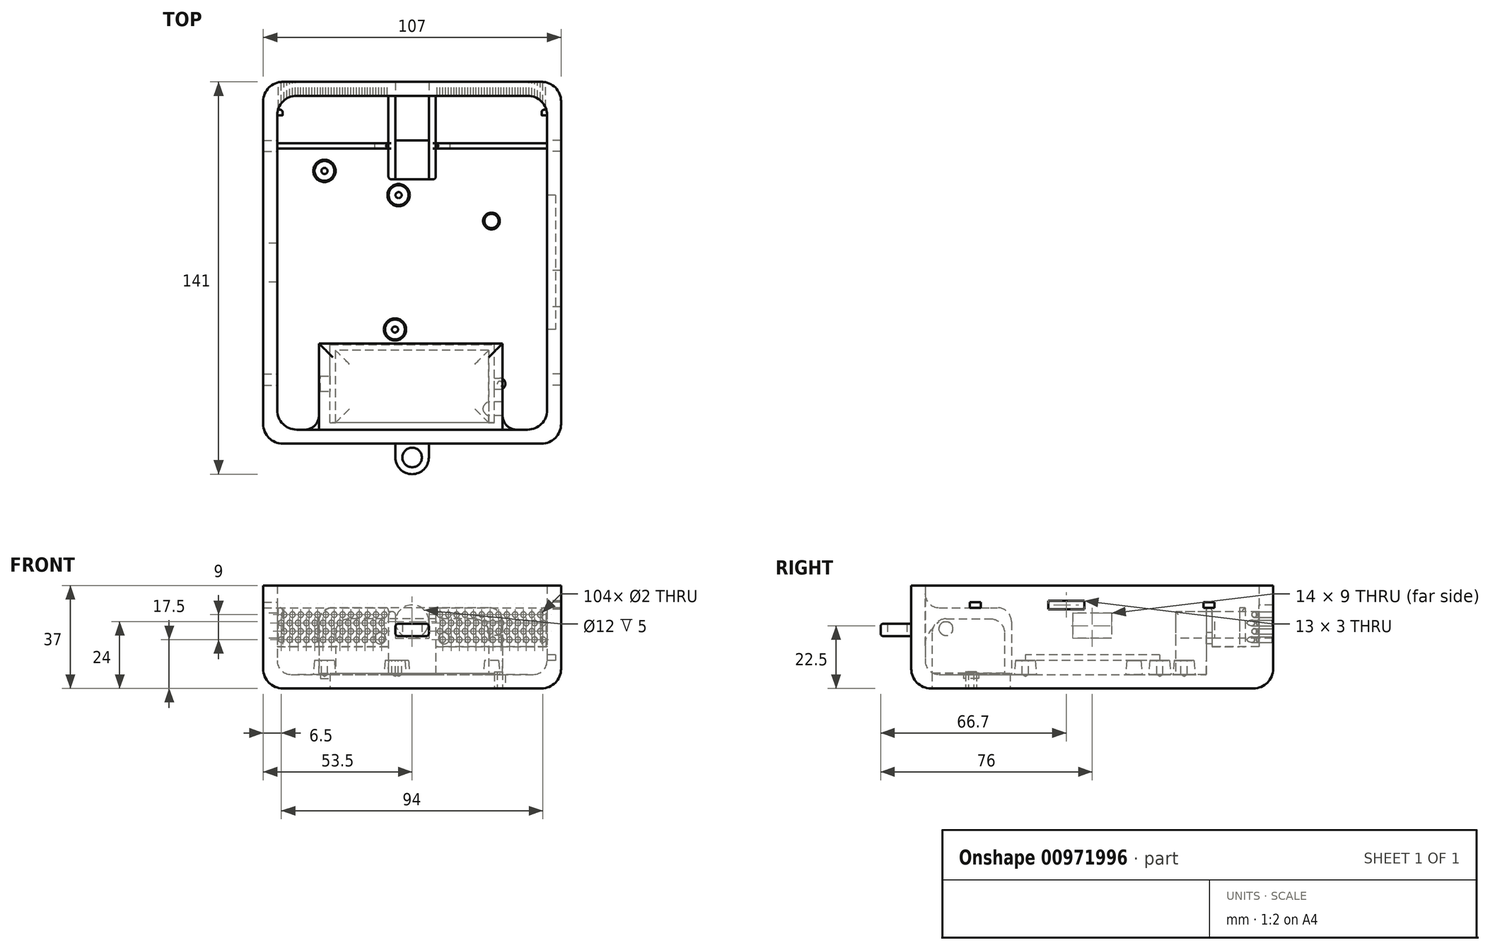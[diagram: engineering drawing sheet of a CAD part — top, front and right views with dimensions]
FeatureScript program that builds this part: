
annotation { "Feature Type Name" : "Feature", "Feature Type Description" : "" }
export const myFeature = defineFeature(function(context is Context, id is Id, definition is map)
    precondition{}
    {
        {
            var Q0;
            Q0=qCreatedBy(makeId("Top.planeOp"),FACE);
            var sketch = newSketch(context, id + "F0", { "sketchPlane" : qUnion([Q0])});
            skLineSegment(sketch, "E0.bottom", {"start": v(48.5, -60) * mm, "end": v(-48.5, -60) * mm});
            skLineSegment(sketch, "E0.top", {"start": v(48.5, 60) * mm, "end": v(-48.5, 60) * mm});
            skLineSegment(sketch, "E0.left", {"start": v(48.5, -60) * mm, "end": v(48.5, 60) * mm});
            skLineSegment(sketch, "E0.right", {"start": v(-48.5, -60) * mm, "end": v(-48.5, 60) * mm});
            skPoint(sketch, "E0.middle", {"position": v(0, 0) * mm});
            skSolve(sketch);
        }
        {
            var Q0;
            Q0 = qSketchRegion(id + "F0", true);
            extrude(context, id + "F1", {"entities" : qUnion([Q0]), "depth" : 32 * mm, "offsetDistance" : 25 * mm});
        }
        {
            var Q0;
            Q0=makeQuery(id+"F1.opExtrude","CAP_FACE",FACE,{"disambiguationData":[OSD([sQuery(id+"F0.wireOp",EDGE,"E0.bottom"),sQuery(id+"F0.wireOp",EDGE,"E0.top"),sQuery(id+"F0.wireOp",EDGE,"E0.left"),sQuery(id+"F0.wireOp",EDGE,"E0.right")])],"isStart":false});
            shell(context, id + "F2", {"entities" : qUnion([Q0]), "thickness" : 5 * mm, "oppositeDirection" : true});
        }
        {
            var Q0;
            Q0=qCreatedBy(makeId("Top.planeOp"),FACE);
            cPlane(context, id + "F3", {"entities" : qUnion([Q0]), "cplaneType" : CPlaneType.OFFSET, "offset" : 16 * mm, "width" : 150 * mm, "height" : 150 * mm});
        }
        {
            var Q0;
            Q0=qCreatedBy(id+"F3.planeOp",FACE);
            var sketch = newSketch(context, id + "F4", { "sketchPlane" : qUnion([Q0])});
            skLineSegment(sketch, "E1.bottom", {"start": v(6, -70) * mm, "end": v(-6, -70) * mm});
            skLineSegment(sketch, "E1.top", {"start": v(6, -65) * mm, "end": v(-6, -65) * mm});
            skLineSegment(sketch, "E1.left", {"start": v(6, -70) * mm, "end": v(6, -65) * mm});
            skLineSegment(sketch, "E1.right", {"start": v(-6, -70) * mm, "end": v(-6, -65) * mm});
            skArc(sketch, "E2", {"start": v(-6, -70) * mm, "mid": v(0, -76) * mm, "end": v(6, -70) * mm});
            skCircle(sketch, "E3", {"center": v(0, -70) * mm, "radius": 3.5 * mm});
            skSolve(sketch);
        }
        {
            var Q0;
            Q0 = qSketchRegion(id + "F4", true);
            extrude(context, id + "F5", {"entities" : qUnion([Q0]), "operationType" : NewBodyOperationType.ADD, "depth" : 2.25 * mm, "offsetDistance" : 25 * mm, "hasSecondDirection" : true, "secondDirectionOppositeDirection" : true, "secondDirectionDepth" : 2.25 * mm});
        }
        {
            var Q0;
            Q0=makeQuery(id+"F2.opShell","OFFSET_FACE",FACE,{"disambiguationData":[OSD([sQuery(id+"F0.wireOp",EDGE,"E0.bottom"),sQuery(id+"F0.wireOp",EDGE,"E0.top"),sQuery(id+"F0.wireOp",EDGE,"E0.left"),sQuery(id+"F0.wireOp",EDGE,"E0.right"),sQuery(id+"F0.wireOp",EDGE,"ri5jnIwm-DSlt-X9KJ-Zgm1-c5zNFrCCeeFj.top"),sQuery(id+"F0.wireOp",EDGE,"ri5jnIwm-DSlt-X9KJ-Zgm1-c5zNFrCCeeFj.left"),sQuery(id+"F0.wireOp",EDGE,"ri5jnIwm-DSlt-X9KJ-Zgm1-c5zNFrCCeeFj.right")])]});
            var sketch = newSketch(context, id + "F6", { "sketchPlane" : qUnion([Q0])});
            skLineSegment(sketch, "E4.bottom", {"start": v(-33.5, -60) * mm, "end": v(32.5, -60) * mm});
            skLineSegment(sketch, "E4.top", {"start": v(-33.5, -29) * mm, "end": v(32.5, -29) * mm});
            skLineSegment(sketch, "E4.left", {"start": v(-33.5, -60) * mm, "end": v(-33.5, -29) * mm});
            skLineSegment(sketch, "E4.right", {"start": v(32.5, -60) * mm, "end": v(32.5, -29) * mm});
            skLineSegment(sketch, "E5.bottom", {"start": v(27.5, -57.5) * mm, "end": v(-27.5, -57.5) * mm});
            skLineSegment(sketch, "E5.top", {"start": v(27.5, -31.5) * mm, "end": v(-27.5, -31.5) * mm});
            skLineSegment(sketch, "E5.left", {"start": v(27.5, -57.5) * mm, "end": v(27.5, -31.5) * mm});
            skLineSegment(sketch, "E5.right", {"start": v(-27.5, -57.5) * mm, "end": v(-27.5, -31.5) * mm});
            skPoint(sketch, "E5.middle", {"position": v(0, -44.5) * mm});
            skPoint(sketch, "E6", {"position": v(-33.5, -44.5) * mm});
            skSolve(sketch);
        }
        {
            var Q0;
            Q0=makeQuery(id+"F6.imprint","IMPRINT",FACE,{"disambiguationData":[TD([[makeQuery(id+"F6.imprint","IMPRINT",EDGE,{"derivedFrom":sQuery(id+"F6.wireOp",EDGE,"E5.bottom")}),-1.0]])]});
            var Q1;
            Q1=makeQuery(id+"F6.imprint","IMPRINT",FACE,{"disambiguationData":[TD([[makeQuery(id+"F6.imprint","IMPRINT",EDGE,{"derivedFrom":sQuery(id+"F6.wireOp",EDGE,"E4.bottom")}),-1.0]])]});
            extrude(context, id + "F7", {"entities" : qUnion([Q0, Q1]), "operationType" : NewBodyOperationType.ADD, "depth" : 24 * mm, "offsetDistance" : 25 * mm});
        }
        {
            var Q0;
            Q0=makeQuery(id+"F6.imprint","IMPRINT",FACE,{"disambiguationData":[TD([[makeQuery(id+"F6.imprint","IMPRINT",EDGE,{"derivedFrom":sQuery(id+"F6.wireOp",EDGE,"E5.bottom")}),-1.0]])]});
            var Q1;
            Q1=makeQuery(id+"F1.opExtrude","CAP_FACE",FACE,{"disambiguationData":[OSD([sQuery(id+"F0.wireOp",EDGE,"E0.bottom"),sQuery(id+"F0.wireOp",EDGE,"E0.top"),sQuery(id+"F0.wireOp",EDGE,"E0.left"),sQuery(id+"F0.wireOp",EDGE,"E0.right"),sQuery(id+"F0.wireOp",EDGE,"ri5jnIwm-DSlt-X9KJ-Zgm1-c5zNFrCCeeFj.top"),sQuery(id+"F0.wireOp",EDGE,"ri5jnIwm-DSlt-X9KJ-Zgm1-c5zNFrCCeeFj.left"),sQuery(id+"F0.wireOp",EDGE,"ri5jnIwm-DSlt-X9KJ-Zgm1-c5zNFrCCeeFj.right")])],"isStart":true});
            extrude(context, id + "F8", {"entities" : qUnion([Q0]), "operationType" : NewBodyOperationType.REMOVE, "depth" : 20 * mm, "offsetDistance" : 25 * mm, "hasSecondDirection" : true, "secondDirectionBound" : SecondDirectionBoundingType.UP_TO_SURFACE, "secondDirectionOppositeDirection" : true, "secondDirectionDepth" : 25 * mm, "secondDirectionBoundEntityFace" : qUnion([Q1])});
        }
        {
            var Q0;
            Q0=makeQuery(id+"F1.opExtrude","CAP_FACE",FACE,{"disambiguationData":[OSD([sQuery(id+"F0.wireOp",EDGE,"E0.bottom"),sQuery(id+"F0.wireOp",EDGE,"E0.top"),sQuery(id+"F0.wireOp",EDGE,"E0.left"),sQuery(id+"F0.wireOp",EDGE,"E0.right")])],"isStart":true});
            var sketch = newSketch(context, id + "F9", { "sketchPlane" : qUnion([Q0])});
            skLineSegment(sketch, "E7.bottom", {"start": v(-29.5, 57.5) * mm, "end": v(29.5, 57.5) * mm});
            skLineSegment(sketch, "E7.top", {"start": v(-29.5, 29.5) * mm, "end": v(29.5, 29.5) * mm});
            skLineSegment(sketch, "E7.left", {"start": v(-29.5, 57.5) * mm, "end": v(-29.5, 29.5) * mm});
            skLineSegment(sketch, "E7.right", {"start": v(29.5, 57.5) * mm, "end": v(29.5, 29.5) * mm});
            skSolve(sketch);
        }
        {
            var Q0;
            Q0 = qSketchRegion(id + "F9", true);
            extrude(context, id + "F10", {"entities" : qUnion([Q0]), "operationType" : NewBodyOperationType.REMOVE, "oppositeDirection" : true, "depth" : 5.5 * mm, "offsetDistance" : 25 * mm});
        }
        {
            var Q0;
            Q0=makeQuery(id+"F10.boolean.opBoolean","COPY",FACE,{"derivedFrom":makeQuery(id+"F10.opExtrude","SWEPT_FACE",FACE,{"disambiguationData":[OSD([sQuery(id+"F9.wireOp",EDGE,"E7.left")])]})});
            var sketch = newSketch(context, id + "F11", { "sketchPlane" : qUnion([Q0])});
            skLineSegment(sketch, "E8.bottom", {"start": v(-40.75, 0.5) * mm, "end": v(-46.25, 0.5) * mm});
            skLineSegment(sketch, "E8.top", {"start": v(-40.75, -1.5) * mm, "end": v(-46.25, -1.5) * mm});
            skLineSegment(sketch, "E8.left", {"start": v(-40.75, 0.5) * mm, "end": v(-40.75, -1.5) * mm});
            skLineSegment(sketch, "E8.right", {"start": v(-46.25, 0.5) * mm, "end": v(-46.25, -1.5) * mm});
            skPoint(sketch, "E9", {"position": v(-43.5, 0.5) * mm});
            skSolve(sketch);
        }
        {
            var Q0;
            Q0 = qSketchRegion(id + "F11", true);
            extrude(context, id + "F12", {"entities" : qUnion([Q0]), "operationType" : NewBodyOperationType.REMOVE, "oppositeDirection" : true, "depth" : 3.5 * mm, "offsetDistance" : 25 * mm});
        }
        {
            var Q0;
            Q0=makeQuery(id+"F1.opExtrude","CAP_FACE",FACE,{"disambiguationData":[OSD([sQuery(id+"F0.wireOp",EDGE,"E0.bottom"),sQuery(id+"F0.wireOp",EDGE,"E0.top"),sQuery(id+"F0.wireOp",EDGE,"E0.left"),sQuery(id+"F0.wireOp",EDGE,"E0.right")])],"isStart":true});
            var sketch = newSketch(context, id + "F13", { "sketchPlane" : qUnion([Q0])});
            skLineSegment(sketch, "E10.bottom", {"start": v(29.5, 45.5) * mm, "end": v(31.5, 45.5) * mm});
            skLineSegment(sketch, "E10.top", {"start": v(29.5, 41.5) * mm, "end": v(31.5, 41.5) * mm});
            skLineSegment(sketch, "E10.left", {"start": v(29.5, 45.5) * mm, "end": v(29.5, 41.5) * mm});
            skLineSegment(sketch, "E10.right", {"start": v(31.5, 45.5) * mm, "end": v(31.5, 41.5) * mm});
            skArc(sketch, "E11", {"start": v(31.5, 41.5) * mm, "mid": v(33.5, 43.5) * mm, "end": v(31.5, 45.5) * mm});
            skCircle(sketch, "E12", {"center": v(31.5, 43.5) * mm, "radius": 0.9 * mm});
            skSolve(sketch);
        }
        {
            var Q0;
            Q0 = qSketchRegion(id + "F13", true);
            var Q1;
            {var subQ0=sQuery(id+"F13.wireOp",EDGE,"E12");var subQ1=sQuery(id+"F13.wireOp",EDGE,"E10.right");var subQ2=makeQuery(id+"F13.imprint","INTERSECT",VERTEX,{"disambiguationData":[OD(0.0)],"derivedFrom":[subQ1,subQ0]});Q1=makeQuery(id+"F13.imprint","IMPRINT",FACE,{"disambiguationData":[TD([[makeQuery(id+"F13.imprint","IMPRINT",EDGE,{"disambiguationData":[TD([[subQ2,-1.0]])],"derivedFrom":subQ1}),-1.0]])]});}
            var Q2;
            {var subQ0=sQuery(id+"F13.wireOp",EDGE,"E12");var subQ1=sQuery(id+"F13.wireOp",EDGE,"E10.right");var subQ2=makeQuery(id+"F13.imprint","INTERSECT",VERTEX,{"disambiguationData":[OD(0.0)],"derivedFrom":[subQ1,subQ0]});Q2=makeQuery(id+"F13.imprint","IMPRINT",FACE,{"disambiguationData":[TD([[makeQuery(id+"F13.imprint","IMPRINT",EDGE,{"disambiguationData":[TD([[subQ2,-1.0]])],"derivedFrom":subQ1}),1.0]])]});}
            extrude(context, id + "F14", {"entities" : qUnion([Q0, Q1, Q2]), "operationType" : NewBodyOperationType.REMOVE, "oppositeDirection" : true, "depth" : 3.5 * mm, "offsetDistance" : 25 * mm});
        }
        {
            var Q0;
            {var subQ0=sQuery(id+"F13.wireOp",EDGE,"E12");var subQ1=sQuery(id+"F13.wireOp",EDGE,"E10.right");var subQ2=makeQuery(id+"F13.imprint","INTERSECT",VERTEX,{"disambiguationData":[OD(0.0)],"derivedFrom":[subQ1,subQ0]});Q0=makeQuery(id+"F13.imprint","IMPRINT",FACE,{"disambiguationData":[TD([[makeQuery(id+"F13.imprint","IMPRINT",EDGE,{"disambiguationData":[TD([[subQ2,-1.0]])],"derivedFrom":subQ1}),-1.0]])]});}
            var Q1;
            {var subQ0=sQuery(id+"F13.wireOp",EDGE,"E12");var subQ1=sQuery(id+"F13.wireOp",EDGE,"E10.right");var subQ2=makeQuery(id+"F13.imprint","INTERSECT",VERTEX,{"disambiguationData":[OD(0.0)],"derivedFrom":[subQ1,subQ0]});Q1=makeQuery(id+"F13.imprint","IMPRINT",FACE,{"disambiguationData":[TD([[makeQuery(id+"F13.imprint","IMPRINT",EDGE,{"disambiguationData":[TD([[subQ2,-1.0]])],"derivedFrom":subQ1}),1.0]])]});}
            var Q2;
            Q2=makeQuery(id+"F2.opShell","OFFSET_FACE",FACE,{"disambiguationData":[OSD([sQuery(id+"F0.wireOp",EDGE,"E0.bottom"),sQuery(id+"F0.wireOp",EDGE,"E0.top"),sQuery(id+"F0.wireOp",EDGE,"E0.left"),sQuery(id+"F0.wireOp",EDGE,"E0.right")])]});
            extrude(context, id + "F15", {"entities" : qUnion([Q0, Q1]), "operationType" : NewBodyOperationType.REMOVE, "oppositeDirection" : true, "depth" : 6 * mm, "endBoundEntityFace" : qUnion([Q2]), "offsetDistance" : 25 * mm});
        }
        {
            var Q0;
            Q0=makeQuery(id+"F2.opShell","OFFSET_FACE",FACE,{"disambiguationData":[OSD([sQuery(id+"F0.wireOp",EDGE,"E0.bottom"),sQuery(id+"F0.wireOp",EDGE,"E0.top"),sQuery(id+"F0.wireOp",EDGE,"E0.left"),sQuery(id+"F0.wireOp",EDGE,"E0.right")])]});
            var sketch = newSketch(context, id + "F16", { "sketchPlane" : qUnion([Q0])});
            skCircle(sketch, "E13", {"center": v(-4.86, 24.3) * mm, "radius": 4 * mm});
            skCircle(sketch, "E14", {"center": v(-6.16, -24) * mm, "radius": 4 * mm});
            skCircle(sketch, "E15", {"center": v(-31.5, 33) * mm, "radius": 4 * mm});
            skCircle(sketch, "E16", {"center": v(28.5, 15) * mm, "radius": 3 * mm});
            skSolve(sketch);
        }
        {
            var Q0;
            Q0 = qSketchRegion(id + "F16", true);
            extrude(context, id + "F17", {"entities" : qUnion([Q0]), "operationType" : NewBodyOperationType.ADD, "depth" : 5 * mm, "offsetDistance" : 25 * mm, "hasDraft" : true, "draftAngle" : 5 * degree, "draftPullDirection" : true});
        }
        {
            var Q0;
            Q0=makeQuery(id+"F17.opExtrude","CAP_FACE",FACE,{"disambiguationData":[OSD([sQuery(id+"F16.wireOp",EDGE,"E13")])],"isStart":false});
            var sketch = newSketch(context, id + "F18", { "sketchPlane" : qUnion([Q0])});
            skPoint(sketch, "E17", {"position": v(-6.16, -24) * mm});
            skPoint(sketch, "E18", {"position": v(-4.86, 24.3) * mm});
            skPoint(sketch, "E19", {"position": v(-31.5, 33) * mm});
            skSolve(sketch);
        }
        {
            var Q0;
            Q0=sQuery(id+"F18.wireOp",VERTEX,"9129957a-feda-4fe3-816d-9d5734e9e23f");
            var Q1;
            Q1=sQuery(id+"F18.wireOp",VERTEX,"4356859b-67c6-456f-994f-b7b154a957ab");
            var Q2;
            Q2=sQuery(id+"F18.wireOp",VERTEX,"E17");
            var Q3;
            Q3=sQuery(id+"F18.wireOp",VERTEX,"E18");
            var Q4;
            Q4=sQuery(id+"F18.wireOp",VERTEX,"E19");
            var Q5;
            Q5=makeQuery(id+"F1.opExtrude","SWEPT_BODY",BODY,{"disambiguationData":[OSD([sQuery(id+"F0.wireOp",EDGE,"E0.bottom"),sQuery(id+"F0.wireOp",EDGE,"E0.top"),sQuery(id+"F0.wireOp",EDGE,"E0.left"),sQuery(id+"F0.wireOp",EDGE,"E0.right")])]});
            hole(context, id + "F19", {"style" : HoleStyle.SIMPLE, "endStyle" : HoleEndStyle.BLIND, "holeDiameter" : 2.2 * mm, "majorDiameter" : 5 * mm, "holeDepth" : 5 * mm, "isTappedThrough" : true, "tappedDepth" : 12 * mm, "tapClearance" : 3, "locations" : qUnion([Q0, Q1, Q2, Q3, Q4]), "scope" : qUnion([Q5])});
        }
        {
            var Q0;
            Q0=makeQuery(id+"F2.opShell","OFFSET_FACE",FACE,{"disambiguationData":[OSD([sQuery(id+"F0.wireOp",EDGE,"E0.left")])]});
            var sketch = newSketch(context, id + "F20", { "sketchPlane" : qUnion([Q0])});
            skLineSegment(sketch, "E20.bottom", {"start": v(-24.3, 7) * mm, "end": v(24, 7) * mm});
            skLineSegment(sketch, "E20.top", {"start": v(-24.3, 5) * mm, "end": v(24, 5) * mm});
            skLineSegment(sketch, "E20.left", {"start": v(-24.3, 7) * mm, "end": v(-24.3, 5) * mm});
            skLineSegment(sketch, "E20.right", {"start": v(24, 7) * mm, "end": v(24, 5) * mm});
            skSolve(sketch);
        }
        {
            var Q0;
            Q0 = qSketchRegion(id + "F20", true);
            extrude(context, id + "F21", {"entities" : qUnion([Q0]), "operationType" : NewBodyOperationType.REMOVE, "oppositeDirection" : true, "depth" : 3 * mm, "offsetDistance" : 25 * mm});
        }
        {
            var Q0;
            Q0=makeQuery(id+"F8.boolean.opBoolean","COPY",FACE,{"derivedFrom":makeQuery(id+"F8.opExtrude","SWEPT_FACE",FACE,{"disambiguationData":[OSD([sQuery(id+"F6.wireOp",EDGE,"E5.left")])]})});
            var sketch = newSketch(context, id + "F22", { "sketchPlane" : qUnion([Q0])});
            skCircle(sketch, "E21", {"center": v(52.5, 16.5) * mm, "radius": 2.5 * mm});
            skSolve(sketch);
        }
        {
            var Q0;
            Q0 = qSketchRegion(id + "F22", true);
            var Q1;
            Q1=makeQuery(id+"F7.opExtrude","SWEPT_FACE",FACE,{"disambiguationData":[OSD([sQuery(id+"F6.wireOp",EDGE,"E4.right")])]});
            extrude(context, id + "F23", {"entities" : qUnion([Q0]), "operationType" : NewBodyOperationType.REMOVE, "endBound" : BoundingType.UP_TO_SURFACE, "oppositeDirection" : true, "depth" : 25 * mm, "endBoundEntityFace" : qUnion([Q1]), "offsetDistance" : 25 * mm});
        }
        {
            var Q0;
            Q0=makeQuery(id+"F2.opShell","OFFSET_FACE",FACE,{"disambiguationData":[OSD([sQuery(id+"F0.wireOp",EDGE,"E0.bottom"),sQuery(id+"F0.wireOp",EDGE,"E0.top"),sQuery(id+"F0.wireOp",EDGE,"E0.left"),sQuery(id+"F0.wireOp",EDGE,"E0.right")])]});
            var sketch = newSketch(context, id + "F24", { "sketchPlane" : qUnion([Q0])});
            skLineSegment(sketch, "E22.bottom", {"start": v(-8.5, 60) * mm, "end": v(-6, 60) * mm});
            skLineSegment(sketch, "E22.top", {"start": v(-8.5, 30) * mm, "end": v(-6, 30) * mm});
            skLineSegment(sketch, "E22.left", {"start": v(-8.5, 60) * mm, "end": v(-8.5, 30) * mm});
            skLineSegment(sketch, "E22.right", {"start": v(-6, 60) * mm, "end": v(-6, 30) * mm});
            skLineSegment(sketch, "E23.bottom", {"start": v(6, 60) * mm, "end": v(8.5, 60) * mm});
            skLineSegment(sketch, "E23.top", {"start": v(6, 30) * mm, "end": v(8.5, 30) * mm});
            skLineSegment(sketch, "E23.left", {"start": v(6, 60) * mm, "end": v(6, 30) * mm});
            skLineSegment(sketch, "E23.right", {"start": v(8.5, 60) * mm, "end": v(8.5, 30) * mm});
            skPoint(sketch, "E24", {"position": v(0, 60) * mm});
            skLineSegment(sketch, "E25.bottom", {"start": v(-8.5, 60) * mm, "end": v(8.5, 60) * mm});
            skLineSegment(sketch, "E25.top", {"start": v(-8.5, 30) * mm, "end": v(8.5, 30) * mm});
            skLineSegment(sketch, "E26", {"start": v(-6, 46) * mm, "end": v(6, 46) * mm});
            skSolve(sketch);
        }
        {
            var Q0;
            {var subQ0=sQuery(id+"F24.wireOp",EDGE,"E25.top");var subQ7=sQuery(id+"F24.wireOp",EDGE,"E25.bottom");Q0=qUnion([makeQuery(id+"F24.imprint","IMPRINT",FACE,{"disambiguationData":[TD([[makeQuery(id+"F24.imprint","IMPRINT",EDGE,{"derivedFrom":subQ7}),1.0]])]}),makeQuery(id+"F24.imprint","IMPRINT",FACE,{"disambiguationData":[TD([[makeQuery(id+"F24.imprint","IMPRINT",EDGE,{"derivedFrom":subQ0}),1.0]])]})]);}
            extrude(context, id + "F25", {"entities" : qUnion([Q0]), "operationType" : NewBodyOperationType.ADD, "depth" : 13 * mm, "offsetDistance" : 25 * mm});
        }
        {
            var Q0;
            {var subQ3=sQuery(id+"F24.wireOp",EDGE,"E22.bottom");Q0=makeQuery(id+"F24.imprint","IMPRINT",FACE,{"disambiguationData":[TD([[makeQuery(id+"F24.imprint","IMPRINT",EDGE,{"derivedFrom":subQ3}),1.0]])]});}
            var Q1;
            {var subQ1=sQuery(id+"F24.wireOp",EDGE,"E23.bottom");Q1=makeQuery(id+"F24.imprint","IMPRINT",FACE,{"disambiguationData":[TD([[makeQuery(id+"F24.imprint","IMPRINT",EDGE,{"derivedFrom":subQ1}),1.0]])]});}
            extrude(context, id + "F26", {"entities" : qUnion([Q0, Q1]), "operationType" : NewBodyOperationType.ADD, "depth" : 22.5 * mm, "offsetDistance" : 25 * mm});
        }
        {
            var Q0;
            Q0=makeQuery(id+"F2.opShell","OFFSET_FACE",FACE,{"disambiguationData":[OSD([sQuery(id+"F0.wireOp",EDGE,"E0.top")])]});
            var sketch = newSketch(context, id + "F27", { "sketchPlane" : qUnion([Q0])});
            skCircle(sketch, "E27", {"center": v(0, 19) * mm, "radius": 6 * mm});
            skSolve(sketch);
        }
        {
            var Q0;
            Q0 = qSketchRegion(id + "F27", true);
            var Q1;
            Q1=makeQuery(id+"F1.opExtrude","SWEPT_BODY",BODY,{"disambiguationData":[OSD([sQuery(id+"F0.wireOp",EDGE,"E0.bottom"),sQuery(id+"F0.wireOp",EDGE,"E0.top"),sQuery(id+"F0.wireOp",EDGE,"E0.left"),sQuery(id+"F0.wireOp",EDGE,"E0.right")])]});
            extrude(context, id + "F28", {"entities" : qUnion([Q0]), "operationType" : NewBodyOperationType.REMOVE, "endBound" : BoundingType.UP_TO_BODY, "oppositeDirection" : true, "depth" : 25 * mm, "endBoundEntityBody" : qUnion([Q1]), "offsetDistance" : 25 * mm});
        }
        {
            var Q0;
            Q0=makeQuery(id+"F2.opShell","OFFSET_FACE",FACE,{"disambiguationData":[OSD([sQuery(id+"F0.wireOp",EDGE,"E0.bottom"),sQuery(id+"F0.wireOp",EDGE,"E0.top"),sQuery(id+"F0.wireOp",EDGE,"E0.left"),sQuery(id+"F0.wireOp",EDGE,"E0.right")])]});
            var sketch = newSketch(context, id + "F29", { "sketchPlane" : qUnion([Q0])});
            skLineSegment(sketch, "E28", {"start": v(-48.5, 43) * mm, "end": v(-8.5, 43) * mm});
            skLineSegment(sketch, "E29", {"start": v(-8.5, 43) * mm, "end": v(-8.5, 60) * mm});
            skLineSegment(sketch, "E30", {"start": v(-8.5, 60) * mm, "end": v(-48.5, 60) * mm});
            skLineSegment(sketch, "E31", {"start": v(-48.5, 60) * mm, "end": v(-48.5, 43) * mm});
            skLineSegment(sketch, "E32", {"start": v(-48.5, 43) * mm, "end": v(-48.5, 41) * mm});
            skLineSegment(sketch, "E33", {"start": v(-48.5, 41) * mm, "end": v(-8.5, 41) * mm});
            skLineSegment(sketch, "E34", {"start": v(-8.5, 41) * mm, "end": v(-8.5, 43) * mm});
            skLineSegment(sketch, "E35", {"start": v(8.5, 43) * mm, "end": v(48.5, 43) * mm});
            skLineSegment(sketch, "E36", {"start": v(48.5, 43) * mm, "end": v(48.5, 60) * mm});
            skLineSegment(sketch, "E37", {"start": v(48.5, 60) * mm, "end": v(8.5, 60) * mm});
            skLineSegment(sketch, "E38", {"start": v(8.5, 60) * mm, "end": v(8.5, 43) * mm});
            skLineSegment(sketch, "E39", {"start": v(8.5, 43) * mm, "end": v(8.5, 41) * mm});
            skLineSegment(sketch, "E40", {"start": v(8.5, 41) * mm, "end": v(48.5, 41) * mm});
            skLineSegment(sketch, "E41", {"start": v(48.5, 41) * mm, "end": v(48.5, 43) * mm});
            skLineSegment(sketch, "E42.bottom", {"start": v(48.5, 55) * mm, "end": v(46.5, 55) * mm});
            skLineSegment(sketch, "E42.top", {"start": v(48.5, 53) * mm, "end": v(46.5, 53) * mm});
            skLineSegment(sketch, "E42.left", {"start": v(48.5, 55) * mm, "end": v(48.5, 53) * mm});
            skLineSegment(sketch, "E42.right", {"start": v(46.5, 55) * mm, "end": v(46.5, 53) * mm});
            skLineSegment(sketch, "E43.bottom", {"start": v(-48.5, 55) * mm, "end": v(-46.5, 55) * mm});
            skLineSegment(sketch, "E43.top", {"start": v(-48.5, 53) * mm, "end": v(-46.5, 53) * mm});
            skLineSegment(sketch, "E43.left", {"start": v(-48.5, 55) * mm, "end": v(-48.5, 53) * mm});
            skLineSegment(sketch, "E43.right", {"start": v(-46.5, 55) * mm, "end": v(-46.5, 53) * mm});
            skSolve(sketch);
        }
        {
            var Q0;
            Q0=makeQuery(id+"F29.imprint","IMPRINT",FACE,{"disambiguationData":[TD([[makeQuery(id+"F29.imprint","IMPRINT",EDGE,{"derivedFrom":sQuery(id+"F29.wireOp",EDGE,"E28")}),-1.0]])]});
            var Q1;
            Q1=makeQuery(id+"F29.imprint","IMPRINT",FACE,{"disambiguationData":[TD([[makeQuery(id+"F29.imprint","IMPRINT",EDGE,{"derivedFrom":sQuery(id+"F29.wireOp",EDGE,"E35")}),-1.0]])]});
            var Q2;
            {var subQ0=sQuery(id+"F29.wireOp",EDGE,"E43.bottom");Q2=makeQuery(id+"F29.imprint","IMPRINT",FACE,{"disambiguationData":[TD([[makeQuery(id+"F29.imprint","IMPRINT",EDGE,{"derivedFrom":subQ0}),-1.0]])]});}
            var Q3;
            {var subQ0=sQuery(id+"F29.wireOp",EDGE,"E42.bottom");Q3=makeQuery(id+"F29.imprint","IMPRINT",FACE,{"disambiguationData":[TD([[makeQuery(id+"F29.imprint","IMPRINT",EDGE,{"derivedFrom":subQ0}),1.0]])]});}
            extrude(context, id + "F30", {"entities" : qUnion([Q0, Q1, Q2, Q3]), "operationType" : NewBodyOperationType.ADD, "depth" : 24 * mm, "offsetDistance" : 25 * mm});
        }
        {
            var Q0;
            {var subQ1=sQuery(id+"F29.wireOp",EDGE,"E28");Q0=makeQuery(id+"F29.imprint","IMPRINT",FACE,{"disambiguationData":[TD([[makeQuery(id+"F29.imprint","IMPRINT",EDGE,{"derivedFrom":subQ1}),1.0]])]});}
            var Q1;
            {var subQ3=sQuery(id+"F29.wireOp",EDGE,"E35");Q1=makeQuery(id+"F29.imprint","IMPRINT",FACE,{"disambiguationData":[TD([[makeQuery(id+"F29.imprint","IMPRINT",EDGE,{"derivedFrom":subQ3}),1.0]])]});}
            extrude(context, id + "F31", {"entities" : qUnion([Q0, Q1]), "operationType" : NewBodyOperationType.ADD, "depth" : 10 * mm, "offsetDistance" : 25 * mm});
        }
        {
            var Q0;
            Q0=makeQuery(id+"F2.opShell","OFFSET_FACE",FACE,{"disambiguationData":[OSD([sQuery(id+"F0.wireOp",EDGE,"E0.left")])]});
            var sketch = newSketch(context, id + "F32", { "sketchPlane" : qUnion([Q0])});
            skLineSegment(sketch, "E44.bottom", {"start": v(2.8, 26.5) * mm, "end": v(15.8, 26.5) * mm});
            skLineSegment(sketch, "E44.top", {"start": v(2.8, 23.5) * mm, "end": v(15.8, 23.5) * mm});
            skLineSegment(sketch, "E44.left", {"start": v(2.8, 26.5) * mm, "end": v(2.8, 23.5) * mm});
            skLineSegment(sketch, "E44.right", {"start": v(15.8, 26.5) * mm, "end": v(15.8, 23.5) * mm});
            skSolve(sketch);
        }
        {
            var Q0;
            Q0 = qSketchRegion(id + "F32", true);
            var Q1;
            Q1=makeQuery(id+"F1.opExtrude","SWEPT_FACE",FACE,{"disambiguationData":[OSD([sQuery(id+"F0.wireOp",EDGE,"E0.left")])]});
            extrude(context, id + "F33", {"entities" : qUnion([Q0]), "operationType" : NewBodyOperationType.REMOVE, "endBound" : BoundingType.UP_TO_SURFACE, "oppositeDirection" : true, "depth" : 25 * mm, "endBoundEntityFace" : qUnion([Q1]), "offsetDistance" : 25 * mm});
        }
        {
            var Q0;
            Q0=makeQuery(id+"F30.opExtrude","SWEPT_FACE",FACE,{"disambiguationData":[OSD([sQuery(id+"F29.wireOp",EDGE,"E33")])]});
            var sketch = newSketch(context, id + "F34", { "sketchPlane" : qUnion([Q0])});
            skCircle(sketch, "E45", {"center": v(-11.5, 13) * mm, "radius": 2 * mm});
            skCircle(sketch, "E46", {"center": v(11.5, 13) * mm, "radius": 2 * mm});
            skSolve(sketch);
        }
        {
            var Q0;
            Q0 = qSketchRegion(id + "F34", true);
            var Q1;
            Q1=makeQuery(id+"F30.opExtrude","SWEPT_FACE",FACE,{"disambiguationData":[OSD([sQuery(id+"F29.wireOp",EDGE,"E28")])]});
            extrude(context, id + "F35", {"entities" : qUnion([Q0]), "operationType" : NewBodyOperationType.REMOVE, "endBound" : BoundingType.UP_TO_SURFACE, "oppositeDirection" : true, "depth" : 25 * mm, "endBoundEntityFace" : qUnion([Q1]), "offsetDistance" : 25 * mm});
        }
        {
            var Q0;
            Q0=makeQuery(id+"F1.opExtrude","SWEPT_FACE",FACE,{"disambiguationData":[OSD([sQuery(id+"F0.wireOp",EDGE,"E0.top")])]});
            var sketch = newSketch(context, id + "F36", { "sketchPlane" : qUnion([Q0])});
            skCircle(sketch, "E47", {"center": v(-46, 21.5) * mm, "radius": 1 * mm});
            skCircle(sketch, "E48", {"center": v(-47, 18.5) * mm, "radius": 1 * mm});
            skCircle(sketch, "E49", {"center": v(-46, 15.5) * mm, "radius": 1 * mm});
            skCircle(sketch, "E50", {"center": v(-47, 12.5) * mm, "radius": 1 * mm});
            skCircle(sketch, "E51.1.0.0", {"center": v(-43, 21.5) * mm, "radius": 1 * mm});
            skCircle(sketch, "E51.1.0.1", {"center": v(-44, 18.5) * mm, "radius": 1 * mm});
            skCircle(sketch, "E51.1.0.2", {"center": v(-43, 15.5) * mm, "radius": 1 * mm});
            skCircle(sketch, "E51.1.0.3", {"center": v(-44, 12.5) * mm, "radius": 1 * mm});
            skCircle(sketch, "E51.2.0.0", {"center": v(-40, 21.5) * mm, "radius": 1 * mm});
            skCircle(sketch, "E51.2.0.1", {"center": v(-41, 18.5) * mm, "radius": 1 * mm});
            skCircle(sketch, "E51.2.0.2", {"center": v(-40, 15.5) * mm, "radius": 1 * mm});
            skCircle(sketch, "E51.2.0.3", {"center": v(-41, 12.5) * mm, "radius": 1 * mm});
            skCircle(sketch, "E51.3.0.0", {"center": v(-37, 21.5) * mm, "radius": 1 * mm});
            skCircle(sketch, "E51.3.0.1", {"center": v(-38, 18.5) * mm, "radius": 1 * mm});
            skCircle(sketch, "E51.3.0.2", {"center": v(-37, 15.5) * mm, "radius": 1 * mm});
            skCircle(sketch, "E51.3.0.3", {"center": v(-38, 12.5) * mm, "radius": 1 * mm});
            skCircle(sketch, "E51.4.0.0", {"center": v(-34, 21.5) * mm, "radius": 1 * mm});
            skCircle(sketch, "E51.4.0.1", {"center": v(-35, 18.5) * mm, "radius": 1 * mm});
            skCircle(sketch, "E51.4.0.2", {"center": v(-34, 15.5) * mm, "radius": 1 * mm});
            skCircle(sketch, "E51.4.0.3", {"center": v(-35, 12.5) * mm, "radius": 1 * mm});
            skCircle(sketch, "E51.5.0.0", {"center": v(-31, 21.5) * mm, "radius": 1 * mm});
            skCircle(sketch, "E51.5.0.1", {"center": v(-32, 18.5) * mm, "radius": 1 * mm});
            skCircle(sketch, "E51.5.0.2", {"center": v(-31, 15.5) * mm, "radius": 1 * mm});
            skCircle(sketch, "E51.5.0.3", {"center": v(-32, 12.5) * mm, "radius": 1 * mm});
            skCircle(sketch, "E51.6.0.0", {"center": v(-28, 21.5) * mm, "radius": 1 * mm});
            skCircle(sketch, "E51.6.0.1", {"center": v(-29, 18.5) * mm, "radius": 1 * mm});
            skCircle(sketch, "E51.6.0.2", {"center": v(-28, 15.5) * mm, "radius": 1 * mm});
            skCircle(sketch, "E51.6.0.3", {"center": v(-29, 12.5) * mm, "radius": 1 * mm});
            skCircle(sketch, "E51.7.0.0", {"center": v(-25, 21.5) * mm, "radius": 1 * mm});
            skCircle(sketch, "E51.7.0.1", {"center": v(-26, 18.5) * mm, "radius": 1 * mm});
            skCircle(sketch, "E51.7.0.2", {"center": v(-25, 15.5) * mm, "radius": 1 * mm});
            skCircle(sketch, "E51.7.0.3", {"center": v(-26, 12.5) * mm, "radius": 1 * mm});
            skCircle(sketch, "E51.8.0.0", {"center": v(-22, 21.5) * mm, "radius": 1 * mm});
            skCircle(sketch, "E51.8.0.1", {"center": v(-23, 18.5) * mm, "radius": 1 * mm});
            skCircle(sketch, "E51.8.0.2", {"center": v(-22, 15.5) * mm, "radius": 1 * mm});
            skCircle(sketch, "E51.8.0.3", {"center": v(-23, 12.5) * mm, "radius": 1 * mm});
            skCircle(sketch, "E51.9.0.0", {"center": v(-19, 21.5) * mm, "radius": 1 * mm});
            skCircle(sketch, "E51.9.0.1", {"center": v(-20, 18.5) * mm, "radius": 1 * mm});
            skCircle(sketch, "E51.9.0.2", {"center": v(-19, 15.5) * mm, "radius": 1 * mm});
            skCircle(sketch, "E51.9.0.3", {"center": v(-20, 12.5) * mm, "radius": 1 * mm});
            skCircle(sketch, "E51.10.0.0", {"center": v(-16, 21.5) * mm, "radius": 1 * mm});
            skCircle(sketch, "E51.10.0.1", {"center": v(-17, 18.5) * mm, "radius": 1 * mm});
            skCircle(sketch, "E51.10.0.2", {"center": v(-16, 15.5) * mm, "radius": 1 * mm});
            skCircle(sketch, "E51.10.0.3", {"center": v(-17, 12.5) * mm, "radius": 1 * mm});
            skCircle(sketch, "E51.11.0.0", {"center": v(-13, 21.5) * mm, "radius": 1 * mm});
            skCircle(sketch, "E51.11.0.1", {"center": v(-14, 18.5) * mm, "radius": 1 * mm});
            skCircle(sketch, "E51.11.0.2", {"center": v(-13, 15.5) * mm, "radius": 1 * mm});
            skCircle(sketch, "E51.11.0.3", {"center": v(-14, 12.5) * mm, "radius": 1 * mm});
            skLineSegment(sketch, "E51.direction1", {"start": v(-46, 21.5) * mm, "end": v(-43, 21.5) * mm, "construction": true});
            skLineSegment(sketch, "E52", {"start": v(0, -5) * mm, "end": v(0, 32) * mm, "construction": true});
            skCircle(sketch, "E53.0.12.0", {"center": v(-10, 21.5) * mm, "radius": 1 * mm});
            skCircle(sketch, "E53.2.12.0", {"center": v(-11, 18.5) * mm, "radius": 1 * mm});
            skCircle(sketch, "E53.4.12.0", {"center": v(-10, 15.5) * mm, "radius": 1 * mm});
            skCircle(sketch, "E53.6.12.0", {"center": v(-11, 12.5) * mm, "radius": 1 * mm});
            skCircle(sketch, "E54.MirrorC", {"center": v(29, 18.5) * mm, "radius": 1 * mm});
            skCircle(sketch, "E55.MirrorC", {"center": v(11, 12.5) * mm, "radius": 1 * mm});
            skCircle(sketch, "E56.MirrorC", {"center": v(26, 18.5) * mm, "radius": 1 * mm});
            skCircle(sketch, "E57.MirrorC", {"center": v(47, 18.5) * mm, "radius": 1 * mm});
            skCircle(sketch, "E58.MirrorC", {"center": v(13, 15.5) * mm, "radius": 1 * mm});
            skCircle(sketch, "E59.MirrorC", {"center": v(40, 15.5) * mm, "radius": 1 * mm});
            skCircle(sketch, "E60.MirrorC", {"center": v(29, 12.5) * mm, "radius": 1 * mm});
            skCircle(sketch, "E61.MirrorC", {"center": v(44, 18.5) * mm, "radius": 1 * mm});
            skCircle(sketch, "E62.MirrorC", {"center": v(37, 15.5) * mm, "radius": 1 * mm});
            skCircle(sketch, "E63.MirrorC", {"center": v(19, 21.5) * mm, "radius": 1 * mm});
            skCircle(sketch, "E64.MirrorC", {"center": v(16, 15.5) * mm, "radius": 1 * mm});
            skCircle(sketch, "E65.MirrorC", {"center": v(14, 12.5) * mm, "radius": 1 * mm});
            skCircle(sketch, "E66.MirrorC", {"center": v(17, 18.5) * mm, "radius": 1 * mm});
            skCircle(sketch, "E67.MirrorC", {"center": v(38, 12.5) * mm, "radius": 1 * mm});
            skCircle(sketch, "E68.MirrorC", {"center": v(40, 21.5) * mm, "radius": 1 * mm});
            skCircle(sketch, "E69.MirrorC", {"center": v(28, 15.5) * mm, "radius": 1 * mm});
            skCircle(sketch, "E70.MirrorC", {"center": v(20, 12.5) * mm, "radius": 1 * mm});
            skCircle(sketch, "E71.MirrorC", {"center": v(43, 15.5) * mm, "radius": 1 * mm});
            skCircle(sketch, "E72.MirrorC", {"center": v(13, 21.5) * mm, "radius": 1 * mm});
            skCircle(sketch, "E73.MirrorC", {"center": v(34, 21.5) * mm, "radius": 1 * mm});
            skCircle(sketch, "E74.MirrorC", {"center": v(32, 12.5) * mm, "radius": 1 * mm});
            skCircle(sketch, "E75.MirrorC", {"center": v(35, 18.5) * mm, "radius": 1 * mm});
            skCircle(sketch, "E76.MirrorC", {"center": v(37, 21.5) * mm, "radius": 1 * mm});
            skCircle(sketch, "E77.MirrorC", {"center": v(41, 18.5) * mm, "radius": 1 * mm});
            skCircle(sketch, "E78.MirrorC", {"center": v(16, 21.5) * mm, "radius": 1 * mm});
            skCircle(sketch, "E79.MirrorC", {"center": v(10, 15.5) * mm, "radius": 1 * mm});
            skCircle(sketch, "E80.MirrorC", {"center": v(43, 21.5) * mm, "radius": 1 * mm});
            skCircle(sketch, "E81.MirrorC", {"center": v(34, 15.5) * mm, "radius": 1 * mm});
            skCircle(sketch, "E82.MirrorC", {"center": v(22, 21.5) * mm, "radius": 1 * mm});
            skLineSegment(sketch, "E83.MirrorCS", {"start": v(46, 21.5) * mm, "end": v(43, 21.5) * mm, "construction": true});
            skCircle(sketch, "E84.MirrorC", {"center": v(47, 12.5) * mm, "radius": 1 * mm});
            skCircle(sketch, "E85.MirrorC", {"center": v(10, 21.5) * mm, "radius": 1 * mm});
            skCircle(sketch, "E86.MirrorC", {"center": v(25, 21.5) * mm, "radius": 1 * mm});
            skCircle(sketch, "E87.MirrorC", {"center": v(11, 18.5) * mm, "radius": 1 * mm});
            skCircle(sketch, "E88.MirrorC", {"center": v(25, 15.5) * mm, "radius": 1 * mm});
            skCircle(sketch, "E89.MirrorC", {"center": v(20, 18.5) * mm, "radius": 1 * mm});
            skCircle(sketch, "E90.MirrorC", {"center": v(41, 12.5) * mm, "radius": 1 * mm});
            skCircle(sketch, "E91.MirrorC", {"center": v(28, 21.5) * mm, "radius": 1 * mm});
            skCircle(sketch, "E92.MirrorC", {"center": v(14, 18.5) * mm, "radius": 1 * mm});
            skCircle(sketch, "E93.MirrorC", {"center": v(19, 15.5) * mm, "radius": 1 * mm});
            skCircle(sketch, "E94.MirrorC", {"center": v(23, 18.5) * mm, "radius": 1 * mm});
            skCircle(sketch, "E95.MirrorC", {"center": v(32, 18.5) * mm, "radius": 1 * mm});
            skCircle(sketch, "E96.MirrorC", {"center": v(38, 18.5) * mm, "radius": 1 * mm});
            skCircle(sketch, "E97.MirrorC", {"center": v(46, 15.5) * mm, "radius": 1 * mm});
            skCircle(sketch, "E98.MirrorC", {"center": v(31, 21.5) * mm, "radius": 1 * mm});
            skCircle(sketch, "E99.MirrorC", {"center": v(31, 15.5) * mm, "radius": 1 * mm});
            skCircle(sketch, "E100.MirrorC", {"center": v(26, 12.5) * mm, "radius": 1 * mm});
            skCircle(sketch, "E101.MirrorC", {"center": v(46, 21.5) * mm, "radius": 1 * mm});
            skCircle(sketch, "E102.MirrorC", {"center": v(17, 12.5) * mm, "radius": 1 * mm});
            skCircle(sketch, "E103.MirrorC", {"center": v(23, 12.5) * mm, "radius": 1 * mm});
            skCircle(sketch, "E104.MirrorC", {"center": v(22, 15.5) * mm, "radius": 1 * mm});
            skCircle(sketch, "E105.MirrorC", {"center": v(44, 12.5) * mm, "radius": 1 * mm});
            skCircle(sketch, "E106.MirrorC", {"center": v(35, 12.5) * mm, "radius": 1 * mm});
            skSolve(sketch);
        }
        {
            var Q0;
            Q0 = qSketchRegion(id + "F36", true);
            var Q1;
            Q1=makeQuery(id+"F30.opExtrude","SWEPT_FACE",FACE,{"disambiguationData":[OSD([sQuery(id+"F29.wireOp",EDGE,"E43.bottom")])]});
            extrude(context, id + "F37", {"entities" : qUnion([Q0]), "operationType" : NewBodyOperationType.REMOVE, "endBound" : BoundingType.UP_TO_SURFACE, "oppositeDirection" : true, "depth" : 25 * mm, "endBoundEntityFace" : qUnion([Q1]), "offsetDistance" : 25 * mm});
        }
        {
            var Q0;
            Q0=makeQuery(id+"F2.opShell","OFFSET_FACE",FACE,{"disambiguationData":[OSD([sQuery(id+"F0.wireOp",EDGE,"E0.left")])]});
            var sketch = newSketch(context, id + "F38", { "sketchPlane" : qUnion([Q0])});
            skLineSegment(sketch, "E107.bottom", {"start": v(-44, 26) * mm, "end": v(-40, 26) * mm});
            skLineSegment(sketch, "E107.top", {"start": v(-44, 24) * mm, "end": v(-40, 24) * mm});
            skLineSegment(sketch, "E107.left", {"start": v(-44, 26) * mm, "end": v(-44, 24) * mm});
            skLineSegment(sketch, "E107.right", {"start": v(-40, 26) * mm, "end": v(-40, 24) * mm});
            skLineSegment(sketch, "E108.bottom", {"start": v(40, 26) * mm, "end": v(44, 26) * mm});
            skLineSegment(sketch, "E108.top", {"start": v(40, 24) * mm, "end": v(44, 24) * mm});
            skLineSegment(sketch, "E108.left", {"start": v(40, 26) * mm, "end": v(40, 24) * mm});
            skLineSegment(sketch, "E108.right", {"start": v(44, 26) * mm, "end": v(44, 24) * mm});
            skSolve(sketch);
        }
        {
            var Q0;
            Q0=makeQuery(id+"F2.opShell","OFFSET_FACE",FACE,{"disambiguationData":[OSD([sQuery(id+"F0.wireOp",EDGE,"E0.right")])]});
            var sketch = newSketch(context, id + "F39", { "sketchPlane" : qUnion([Q0])});
            skLineSegment(sketch, "E109.bottom", {"start": v(40, 26) * mm, "end": v(44, 26) * mm});
            skLineSegment(sketch, "E109.top", {"start": v(40, 24) * mm, "end": v(44, 24) * mm});
            skLineSegment(sketch, "E109.left", {"start": v(40, 26) * mm, "end": v(40, 24) * mm});
            skLineSegment(sketch, "E109.right", {"start": v(44, 26) * mm, "end": v(44, 24) * mm});
            skLineSegment(sketch, "E110.bottom", {"start": v(-44, 26) * mm, "end": v(-40, 26) * mm});
            skLineSegment(sketch, "E110.top", {"start": v(-44, 24) * mm, "end": v(-40, 24) * mm});
            skLineSegment(sketch, "E110.left", {"start": v(-44, 26) * mm, "end": v(-44, 24) * mm});
            skLineSegment(sketch, "E110.right", {"start": v(-40, 26) * mm, "end": v(-40, 24) * mm});
            skSolve(sketch);
        }
        {
            var Q0;
            Q0 = qSketchRegion(id + "F38", true);
            var Q1;
            Q1=makeQuery(id+"F1.opExtrude","SWEPT_FACE",FACE,{"disambiguationData":[OSD([sQuery(id+"F0.wireOp",EDGE,"E0.left")])]});
            extrude(context, id + "F40", {"entities" : qUnion([Q0]), "operationType" : NewBodyOperationType.REMOVE, "endBound" : BoundingType.UP_TO_SURFACE, "oppositeDirection" : true, "depth" : 25 * mm, "endBoundEntityFace" : qUnion([Q1]), "offsetDistance" : 25 * mm});
        }
        {
            var Q0;
            Q0 = qSketchRegion(id + "F39", true);
            var Q1;
            Q1=makeQuery(id+"F1.opExtrude","SWEPT_FACE",FACE,{"disambiguationData":[OSD([sQuery(id+"F0.wireOp",EDGE,"E0.right")])]});
            extrude(context, id + "F41", {"entities" : qUnion([Q0]), "operationType" : NewBodyOperationType.REMOVE, "endBound" : BoundingType.UP_TO_SURFACE, "oppositeDirection" : true, "depth" : 25 * mm, "endBoundEntityFace" : qUnion([Q1]), "offsetDistance" : 25 * mm});
        }
        {
            var Q0;
            Q0=makeQuery(id+"F1.opExtrude","SWEPT_FACE",FACE,{"disambiguationData":[OSD([sQuery(id+"F0.wireOp",EDGE,"E0.right")])]});
            var sketch = newSketch(context, id + "F42", { "sketchPlane" : qUnion([Q0])});
            skLineSegment(sketch, "E111.bottom", {"start": v(7, 13) * mm, "end": v(-7, 13) * mm});
            skLineSegment(sketch, "E111.top", {"start": v(7, 22) * mm, "end": v(-7, 22) * mm});
            skLineSegment(sketch, "E111.left", {"start": v(7, 13) * mm, "end": v(7, 22) * mm});
            skLineSegment(sketch, "E111.right", {"start": v(-7, 13) * mm, "end": v(-7, 22) * mm});
            skPoint(sketch, "E111.middle", {"position": v(0, 17.5) * mm});
            skSolve(sketch);
        }
        {
            var Q0;
            Q0=makeQuery(id+"F42.imprint","IMPRINT",FACE,{"disambiguationData":[TD([[makeQuery(id+"F42.imprint","IMPRINT",EDGE,{"derivedFrom":sQuery(id+"F42.wireOp",EDGE,"E111.bottom")}),-1.0]])]});
            var Q1;
            Q1=makeQuery(id+"F2.opShell","OFFSET_FACE",FACE,{"disambiguationData":[OSD([sQuery(id+"F0.wireOp",EDGE,"E0.right")])]});
            extrude(context, id + "F43", {"entities" : qUnion([Q0]), "operationType" : NewBodyOperationType.REMOVE, "endBound" : BoundingType.UP_TO_SURFACE, "oppositeDirection" : true, "depth" : 25 * mm, "endBoundEntityFace" : qUnion([Q1]), "offsetDistance" : 25 * mm});
        }
        {
            var Q0;
            Q0=makeQuery(id+"F7.opExtrude","CAP_EDGE",EDGE,{"disambiguationData":[OSD([sQuery(id+"F6.wireOp",EDGE,"E4.right")])],"isStart":true});
            var Q1;
            {var subQ0=sQuery(id+"F0.wireOp",EDGE,"E0.bottom");var subQ1=sQuery(id+"F0.wireOp",EDGE,"E0.left");Q1=makeQuery(id+"F7.boolean.opBoolean","SPLIT",EDGE,{"disambiguationData":[TD([makeQuery(id+"F2.opShell","OFFSET_FACE",FACE,{"disambiguationData":[OSD([subQ1])]})])],"derivedFrom":makeQuery(id+"F2.opShell","OFFSET_EDGE",EDGE,{"disambiguationData":[OSD([subQ0]),TDD([makeQuery(id+"F1.opExtrude","CAP_EDGE",EDGE,{"disambiguationData":[OSD([subQ0])],"isStart":true})])]})});}
            var Q2;
            {var subQ0=sQuery(id+"F0.wireOp",EDGE,"E0.left");Q2=makeQuery(id+"F17.boolean.opBoolean","SPLIT",EDGE,{"disambiguationData":[TD([makeQuery(id+"F2.opShell","OFFSET_FACE",FACE,{"disambiguationData":[OSD([sQuery(id+"F0.wireOp",EDGE,"E0.bottom"),sQuery(id+"F0.wireOp",EDGE,"E0.top"),subQ0,sQuery(id+"F0.wireOp",EDGE,"E0.right")])]}),makeQuery(id+"F2.opShell","OFFSET_FACE",FACE,{"disambiguationData":[OSD([subQ0])]}),makeQuery(id+"F17.opExtrude","SWEPT_FACE",FACE,{"disambiguationData":[OSD([sQuery(id+"F16.wireOp",EDGE,"LAxlxx99-QZ8O-4oEx-Lo3F-cM2nN16unp1Z")])]}),makeQuery(id+"F17.opExtrude","SWEPT_FACE",FACE,{"disambiguationData":[OSD([sQuery(id+"F16.wireOp",EDGE,"NOKp8BI3-C5vD-0323-3AgK-PuaL4R6wZHdd")])]})])],"derivedFrom":makeQuery(id+"F2.opShell","OFFSET_EDGE",EDGE,{"disambiguationData":[OSD([subQ0]),TDD([makeQuery(id+"F1.opExtrude","CAP_EDGE",EDGE,{"disambiguationData":[OSD([subQ0])],"isStart":true})])]})});}
            var Q3;
            {var subQ0=sQuery(id+"F0.wireOp",EDGE,"E0.bottom");var subQ1=sQuery(id+"F0.wireOp",EDGE,"E0.left");Q3=makeQuery(id+"F17.boolean.opBoolean","SPLIT",EDGE,{"disambiguationData":[TD([makeQuery(id+"F2.opShell","OFFSET_FACE",FACE,{"disambiguationData":[OSD([subQ0])]}),makeQuery(id+"F2.opShell","OFFSET_FACE",FACE,{"disambiguationData":[OSD([subQ0,sQuery(id+"F0.wireOp",EDGE,"E0.top"),subQ1,sQuery(id+"F0.wireOp",EDGE,"E0.right")])]}),makeQuery(id+"F2.opShell","OFFSET_FACE",FACE,{"disambiguationData":[OSD([subQ1])]}),makeQuery(id+"F17.opExtrude","SWEPT_FACE",FACE,{"disambiguationData":[OSD([sQuery(id+"F16.wireOp",EDGE,"NOKp8BI3-C5vD-0323-3AgK-PuaL4R6wZHdd")])]})])],"derivedFrom":makeQuery(id+"F2.opShell","OFFSET_EDGE",EDGE,{"disambiguationData":[OSD([subQ1]),TDD([makeQuery(id+"F1.opExtrude","CAP_EDGE",EDGE,{"disambiguationData":[OSD([subQ1])],"isStart":true})])]})});}
            var Q4;
            {var subQ0=sQuery(id+"F0.wireOp",EDGE,"E0.left");var subQ1=sQuery(id+"F0.wireOp",EDGE,"E0.top");var subQ2=makeQuery(id+"F2.opShell","OFFSET_FACE",FACE,{"disambiguationData":[OSD([sQuery(id+"F0.wireOp",EDGE,"E0.bottom"),subQ1,subQ0,sQuery(id+"F0.wireOp",EDGE,"E0.right")])]});var subQ3=makeQuery(id+"F2.opShell","OFFSET_FACE",FACE,{"disambiguationData":[OSD([subQ0])]});var subQ4=makeQuery(id+"F17.opExtrude","SWEPT_FACE",FACE,{"disambiguationData":[OSD([sQuery(id+"F16.wireOp",EDGE,"LAxlxx99-QZ8O-4oEx-Lo3F-cM2nN16unp1Z")])]});Q4=makeQuery(id+"F30.boolean.opBoolean","SPLIT",EDGE,{"disambiguationData":[TD([subQ4])],"derivedFrom":makeQuery(id+"F17.boolean.opBoolean","SPLIT",EDGE,{"disambiguationData":[TD([subQ2,makeQuery(id+"F2.opShell","OFFSET_FACE",FACE,{"disambiguationData":[OSD([subQ1])]}),subQ3,subQ4])],"derivedFrom":makeQuery(id+"F2.opShell","OFFSET_EDGE",EDGE,{"disambiguationData":[OSD([subQ0]),TDD([makeQuery(id+"F1.opExtrude","CAP_EDGE",EDGE,{"disambiguationData":[OSD([subQ0])],"isStart":true})])]})})});}
            var Q5;
            Q5=makeQuery(id+"F30.opExtrude","CAP_EDGE",EDGE,{"disambiguationData":[OSD([sQuery(id+"F29.wireOp",EDGE,"E40")])],"isStart":true});
            var Q6;
            {var subQ0=sQuery(id+"F0.wireOp",EDGE,"E0.top");var subQ1=sQuery(id+"F0.wireOp",EDGE,"E0.left");Q6=makeQuery(id+"F30.boolean.opBoolean","SPLIT",FACE,{"disambiguationData":[TD([makeQuery(id+"F30.opExtrude","SWEPT_FACE",FACE,{"disambiguationData":[OSD([sQuery(id+"F29.wireOp",EDGE,"E35")])]})])],"derivedFrom":makeQuery(id+"F2.opShell","OFFSET_FACE",FACE,{"disambiguationData":[OSD([sQuery(id+"F0.wireOp",EDGE,"E0.bottom"),subQ0,subQ1,sQuery(id+"F0.wireOp",EDGE,"E0.right")])]})});}
            var Q7;
            {var subQ0=sQuery(id+"F0.wireOp",EDGE,"E0.top");var subQ1=sQuery(id+"F0.wireOp",EDGE,"E0.right");Q7=makeQuery(id+"F30.boolean.opBoolean","SPLIT",FACE,{"disambiguationData":[TD([makeQuery(id+"F30.opExtrude","SWEPT_FACE",FACE,{"disambiguationData":[OSD([sQuery(id+"F29.wireOp",EDGE,"E28")])]})])],"derivedFrom":makeQuery(id+"F2.opShell","OFFSET_FACE",FACE,{"disambiguationData":[OSD([sQuery(id+"F0.wireOp",EDGE,"E0.bottom"),subQ0,sQuery(id+"F0.wireOp",EDGE,"E0.left"),subQ1])]})});}
            var Q8;
            {var subQ0=sQuery(id+"F24.wireOp",EDGE,"E23.right");Q8=makeQuery(id+"F30.boolean.opBoolean","SPLIT",EDGE,{"disambiguationData":[TD([makeQuery(id+"F25.opExtrude","SWEPT_FACE",FACE,{"disambiguationData":[OSD([sQuery(id+"F24.wireOp",EDGE,"E25.top")])]})])],"derivedFrom":makeQuery(id+"F26.opExtrude","CAP_EDGE",EDGE,{"disambiguationData":[OSD([subQ0])],"isStart":true})});}
            var Q9;
            Q9=makeQuery(id+"F26.boolean.opBoolean","MERGE",EDGE,{"derivedFrom":[makeQuery(id+"F25.opExtrude","CAP_EDGE",EDGE,{"disambiguationData":[OSD([sQuery(id+"F24.wireOp",EDGE,"E25.top")])],"isStart":true}),makeQuery(id+"F26.opExtrude","CAP_EDGE",EDGE,{"disambiguationData":[OSD([sQuery(id+"F24.wireOp",EDGE,"E22.top")])],"isStart":true}),makeQuery(id+"F26.opExtrude","CAP_EDGE",EDGE,{"disambiguationData":[OSD([sQuery(id+"F24.wireOp",EDGE,"E23.top")])],"isStart":true})]});
            var Q10;
            {var subQ0=sQuery(id+"F24.wireOp",EDGE,"E22.left");Q10=makeQuery(id+"F30.boolean.opBoolean","SPLIT",EDGE,{"disambiguationData":[TD([makeQuery(id+"F25.opExtrude","SWEPT_FACE",FACE,{"disambiguationData":[OSD([sQuery(id+"F24.wireOp",EDGE,"E25.top")])]})])],"derivedFrom":makeQuery(id+"F26.opExtrude","CAP_EDGE",EDGE,{"disambiguationData":[OSD([subQ0])],"isStart":true})});}
            var Q11;
            Q11=makeQuery(id+"F30.opExtrude","CAP_EDGE",EDGE,{"disambiguationData":[OSD([sQuery(id+"F29.wireOp",EDGE,"E33")])],"isStart":true});
            var Q12;
            {var subQ0=sQuery(id+"F0.wireOp",EDGE,"E0.bottom");var subQ1=sQuery(id+"F0.wireOp",EDGE,"E0.right");Q12=makeQuery(id+"F30.boolean.opBoolean","SPLIT",EDGE,{"disambiguationData":[TD([makeQuery(id+"F2.opShell","OFFSET_FACE",FACE,{"disambiguationData":[OSD([subQ0])]})])],"derivedFrom":makeQuery(id+"F2.opShell","OFFSET_EDGE",EDGE,{"disambiguationData":[OSD([subQ1]),TDD([makeQuery(id+"F1.opExtrude","CAP_EDGE",EDGE,{"disambiguationData":[OSD([subQ1])],"isStart":true})])]})});}
            var Q13;
            {var subQ0=sQuery(id+"F6.wireOp",EDGE,"E4.top");Q13=makeQuery(id+"F17.boolean.opBoolean","SPLIT",EDGE,{"disambiguationData":[TD([makeQuery(id+"F7.opExtrude","SWEPT_FACE",FACE,{"disambiguationData":[OSD([sQuery(id+"F6.wireOp",EDGE,"E4.left")])]})])],"derivedFrom":makeQuery(id+"F7.opExtrude","CAP_EDGE",EDGE,{"disambiguationData":[OSD([subQ0])],"isStart":true})});}
            var Q14;
            Q14=makeQuery(id+"F7.opExtrude","CAP_EDGE",EDGE,{"disambiguationData":[OSD([sQuery(id+"F6.wireOp",EDGE,"E4.left")])],"isStart":true});
            var Q15;
            {var subQ0=sQuery(id+"F0.wireOp",EDGE,"E0.bottom");var subQ1=sQuery(id+"F0.wireOp",EDGE,"E0.right");Q15=makeQuery(id+"F7.boolean.opBoolean","SPLIT",EDGE,{"disambiguationData":[TD([makeQuery(id+"F2.opShell","OFFSET_FACE",FACE,{"disambiguationData":[OSD([subQ1])]})])],"derivedFrom":makeQuery(id+"F2.opShell","OFFSET_EDGE",EDGE,{"disambiguationData":[OSD([subQ0]),TDD([makeQuery(id+"F1.opExtrude","CAP_EDGE",EDGE,{"disambiguationData":[OSD([subQ0])],"isStart":true})])]})});}
            var Q16;
            Q16=makeQuery(id+"F7.opExtrude","CAP_FACE",FACE,{"disambiguationData":[OSD([sQuery(id+"F6.wireOp",EDGE,"E4.bottom"),sQuery(id+"F6.wireOp",EDGE,"E4.top"),sQuery(id+"F6.wireOp",EDGE,"E4.left"),sQuery(id+"F6.wireOp",EDGE,"E4.right")])],"isStart":false});
            var Q17;
            Q17=makeQuery(id+"F8.boolean.opBoolean","COPY",FACE,{"derivedFrom":makeQuery(id+"F8.opExtrude","CAP_FACE",FACE,{"disambiguationData":[OSD([sQuery(id+"F6.wireOp",EDGE,"E5.bottom"),sQuery(id+"F6.wireOp",EDGE,"E5.top"),sQuery(id+"F6.wireOp",EDGE,"E5.left"),sQuery(id+"F6.wireOp",EDGE,"E5.right")])],"isStart":false})});
            var Q18;
            Q18=makeQuery(id+"F5.opExtrude","CAP_EDGE",EDGE,{"disambiguationData":[OSD([sQuery(id+"F4.wireOp",EDGE,"E1.top")])],"isStart":false});
            var Q19;
            Q19=makeQuery(id+"F5.opExtrude","SWEPT_EDGE",EDGE,{"disambiguationData":[OSD([sQuery(id+"F4.wireOp",EDGE,"E1.top"),sQuery(id+"F4.wireOp",EDGE,"E1.right")])]});
            var Q20;
            Q20=makeQuery(id+"F5.opExtrude","CAP_EDGE",EDGE,{"disambiguationData":[OSD([sQuery(id+"F4.wireOp",EDGE,"E1.top")])],"isStart":true});
            var Q21;
            Q21=makeQuery(id+"F5.opExtrude","SWEPT_EDGE",EDGE,{"disambiguationData":[OSD([sQuery(id+"F4.wireOp",EDGE,"E1.top"),sQuery(id+"F4.wireOp",EDGE,"E1.left")])]});
            var Q22;
            Q22=makeQuery(id+"F33.boolean.opBoolean","COPY",EDGE,{"derivedFrom":makeQuery(id+"F33.opExtrude","CAP_EDGE",EDGE,{"disambiguationData":[OSD([sQuery(id+"F32.wireOp",EDGE,"E44.bottom")])],"isStart":false})});
            var Q23;
            Q23=makeQuery(id+"F33.boolean.opBoolean","COPY",EDGE,{"derivedFrom":makeQuery(id+"F33.opExtrude","CAP_EDGE",EDGE,{"disambiguationData":[OSD([sQuery(id+"F32.wireOp",EDGE,"E44.right")])],"isStart":false})});
            var Q24;
            Q24=makeQuery(id+"F33.boolean.opBoolean","COPY",EDGE,{"derivedFrom":makeQuery(id+"F33.opExtrude","CAP_EDGE",EDGE,{"disambiguationData":[OSD([sQuery(id+"F32.wireOp",EDGE,"E44.top")])],"isStart":false})});
            var Q25;
            Q25=makeQuery(id+"F33.boolean.opBoolean","COPY",EDGE,{"derivedFrom":makeQuery(id+"F33.opExtrude","CAP_EDGE",EDGE,{"disambiguationData":[OSD([sQuery(id+"F32.wireOp",EDGE,"E44.left")])],"isStart":false})});
            var Q26;
            Q26=makeQuery(id+"F28.boolean.opBoolean","COPY",EDGE,{"derivedFrom":makeQuery(id+"F28.opExtrude","CAP_EDGE",EDGE,{"disambiguationData":[OSD([sQuery(id+"F27.wireOp",EDGE,"E27")])],"isStart":false})});
            fillet(context, id + "F44", {"entities" : qUnion([Q0, Q1, Q2, Q3, Q4, Q5, Q6, Q7, Q8, Q9, Q10, Q11, Q12, Q13, Q14, Q15, Q16, Q17, Q18, Q19, Q20, Q21, Q22, Q23, Q24, Q25, Q26]), "radius" : 5 * mm, "tangentPropagation" : true, "allowEdgeOverflow" : false});
        }
        {
            var Q0;
            Q0=makeQuery(id+"F30.opExtrude","CAP_EDGE",EDGE,{"disambiguationData":[OSD([sQuery(id+"F29.wireOp",EDGE,"E33")])],"isStart":false});
            var Q1;
            Q1=makeQuery(id+"F30.opExtrude","CAP_EDGE",EDGE,{"disambiguationData":[OSD([sQuery(id+"F29.wireOp",EDGE,"E28")])],"isStart":false});
            var Q2;
            Q2=makeQuery(id+"F26.opExtrude","CAP_EDGE",EDGE,{"disambiguationData":[OSD([sQuery(id+"F24.wireOp",EDGE,"E23.left")])],"isStart":false});
            var Q3;
            Q3=makeQuery(id+"F26.opExtrude","CAP_EDGE",EDGE,{"disambiguationData":[OSD([sQuery(id+"F24.wireOp",EDGE,"E22.right")])],"isStart":false});
            var Q4;
            Q4=makeQuery(id+"F26.opExtrude","SWEPT_EDGE",EDGE,{"disambiguationData":[OSD([sQuery(id+"F24.wireOp",EDGE,"E23.top"),sQuery(id+"F24.wireOp",EDGE,"E23.right")])]});
            var Q5;
            Q5=makeQuery(id+"F26.opExtrude","SWEPT_EDGE",EDGE,{"disambiguationData":[OSD([sQuery(id+"F24.wireOp",EDGE,"E22.top"),sQuery(id+"F24.wireOp",EDGE,"E22.left")])]});
            var Q6;
            Q6=makeQuery(id+"F30.opExtrude","CAP_EDGE",EDGE,{"disambiguationData":[OSD([sQuery(id+"F29.wireOp",EDGE,"E35")])],"isStart":false});
            var Q7;
            Q7=makeQuery(id+"F30.opExtrude","CAP_EDGE",EDGE,{"disambiguationData":[OSD([sQuery(id+"F29.wireOp",EDGE,"E40")])],"isStart":false});
            var Q8;
            {var subQ0=sQuery(id+"F24.wireOp",EDGE,"E22.left");var subQ1=makeQuery(id+"F26.opExtrude","SWEPT_FACE",FACE,{"disambiguationData":[OSD([subQ0])]});var subQ2=sQuery(id+"F24.wireOp",EDGE,"E22.top");var subQ3=makeQuery(id+"F26.opExtrude","CAP_FACE",FACE,{"disambiguationData":[OSD([sQuery(id+"F24.wireOp",EDGE,"E22.bottom"),subQ2,subQ0,sQuery(id+"F24.wireOp",EDGE,"E22.right")])],"isStart":false});Q8=makeQuery(id+"F30.boolean.opBoolean","SPLIT",EDGE,{"disambiguationData":[topologyDisambiguationEdgeConnected([subQ3,subQ1]),TD([makeQuery(id+"F25.opExtrude","SWEPT_FACE",FACE,{"disambiguationData":[OSD([sQuery(id+"F24.wireOp",EDGE,"E25.top")])]})])],"derivedFrom":makeQuery(id+"F26.opExtrude","CAP_EDGE",EDGE,{"disambiguationData":[OSD([subQ0])],"isStart":false})});}
            var Q9;
            {var subQ0=sQuery(id+"F24.wireOp",EDGE,"E22.left");var subQ1=makeQuery(id+"F26.opExtrude","SWEPT_FACE",FACE,{"disambiguationData":[OSD([subQ0])]});var subQ2=makeQuery(id+"F26.opExtrude","CAP_FACE",FACE,{"disambiguationData":[OSD([sQuery(id+"F24.wireOp",EDGE,"E22.bottom"),sQuery(id+"F24.wireOp",EDGE,"E22.top"),subQ0,sQuery(id+"F24.wireOp",EDGE,"E22.right")])],"isStart":false});Q9=makeQuery(id+"F30.boolean.opBoolean","SPLIT",EDGE,{"disambiguationData":[topologyDisambiguationEdgeConnected([subQ2,subQ1]),TD([makeQuery(id+"F2.opShell","OFFSET_FACE",FACE,{"disambiguationData":[OSD([sQuery(id+"F0.wireOp",EDGE,"E0.top")])]})])],"derivedFrom":makeQuery(id+"F26.opExtrude","CAP_EDGE",EDGE,{"disambiguationData":[OSD([subQ0])],"isStart":false})});}
            var Q10;
            {var subQ0=sQuery(id+"F24.wireOp",EDGE,"E23.top");var subQ1=sQuery(id+"F24.wireOp",EDGE,"E23.right");var subQ2=makeQuery(id+"F26.opExtrude","CAP_FACE",FACE,{"disambiguationData":[OSD([sQuery(id+"F24.wireOp",EDGE,"E23.bottom"),subQ0,sQuery(id+"F24.wireOp",EDGE,"E23.left"),subQ1])],"isStart":false});var subQ3=makeQuery(id+"F26.opExtrude","SWEPT_FACE",FACE,{"disambiguationData":[OSD([subQ1])]});Q10=makeQuery(id+"F30.boolean.opBoolean","SPLIT",EDGE,{"disambiguationData":[topologyDisambiguationEdgeConnected([subQ2,subQ3]),TD([makeQuery(id+"F25.opExtrude","SWEPT_FACE",FACE,{"disambiguationData":[OSD([sQuery(id+"F24.wireOp",EDGE,"E25.top")])]})])],"derivedFrom":makeQuery(id+"F26.opExtrude","CAP_EDGE",EDGE,{"disambiguationData":[OSD([subQ1])],"isStart":false})});}
            var Q11;
            {var subQ0=sQuery(id+"F24.wireOp",EDGE,"E23.right");var subQ1=makeQuery(id+"F26.opExtrude","SWEPT_FACE",FACE,{"disambiguationData":[OSD([subQ0])]});var subQ2=makeQuery(id+"F26.opExtrude","CAP_FACE",FACE,{"disambiguationData":[OSD([sQuery(id+"F24.wireOp",EDGE,"E23.bottom"),sQuery(id+"F24.wireOp",EDGE,"E23.top"),sQuery(id+"F24.wireOp",EDGE,"E23.left"),subQ0])],"isStart":false});Q11=makeQuery(id+"F30.boolean.opBoolean","SPLIT",EDGE,{"disambiguationData":[topologyDisambiguationEdgeConnected([subQ2,subQ1]),TD([makeQuery(id+"F2.opShell","OFFSET_FACE",FACE,{"disambiguationData":[OSD([sQuery(id+"F0.wireOp",EDGE,"E0.top")])]})])],"derivedFrom":makeQuery(id+"F26.opExtrude","CAP_EDGE",EDGE,{"disambiguationData":[OSD([subQ0])],"isStart":false})});}
            var Q12;
            Q12=makeQuery(id+"F30.opExtrude","CAP_EDGE",EDGE,{"disambiguationData":[OSD([sQuery(id+"F29.wireOp",EDGE,"E34")])],"isStart":false});
            var Q13;
            Q13=makeQuery(id+"F30.opExtrude","CAP_EDGE",EDGE,{"disambiguationData":[OSD([sQuery(id+"F29.wireOp",EDGE,"E39")])],"isStart":false});
            var Q14;
            Q14=makeQuery(id+"F5.opExtrude","CAP_EDGE",EDGE,{"disambiguationData":[OSD([sQuery(id+"F4.wireOp",EDGE,"E2")])],"isStart":false});
            var Q15;
            Q15=makeQuery(id+"F5.opExtrude","CAP_EDGE",EDGE,{"disambiguationData":[OSD([sQuery(id+"F4.wireOp",EDGE,"E2")])],"isStart":true});
            var Q16;
            Q16=makeQuery(id+"F44.opFillet","BLEND_EDGE",EDGE,{"blendedFrom":[makeQuery(id+"F5.opExtrude","CAP_EDGE",EDGE,{"disambiguationData":[OSD([sQuery(id+"F4.wireOp",EDGE,"E1.top")])],"isStart":false}),makeQuery(id+"F5.opExtrude","SWEPT_FACE",FACE,{"disambiguationData":[OSD([sQuery(id+"F4.wireOp",EDGE,"E3")])]})],"blendedInto":[makeQuery(id+"F5.opExtrude","SWEPT_FACE",FACE,{"disambiguationData":[OSD([sQuery(id+"F4.wireOp",EDGE,"E3")])]})]});
            var Q17;
            Q17=makeQuery(id+"F44.opFillet","BLEND_EDGE",EDGE,{"blendedFrom":[makeQuery(id+"F5.opExtrude","CAP_EDGE",EDGE,{"disambiguationData":[OSD([sQuery(id+"F4.wireOp",EDGE,"E1.top")])],"isStart":true}),makeQuery(id+"F5.opExtrude","SWEPT_FACE",FACE,{"disambiguationData":[OSD([sQuery(id+"F4.wireOp",EDGE,"E3")])]})],"blendedInto":[makeQuery(id+"F5.opExtrude","SWEPT_FACE",FACE,{"disambiguationData":[OSD([sQuery(id+"F4.wireOp",EDGE,"E3")])]})]});
            var Q18;
            Q18=makeQuery(id+"F37.boolean.opBoolean","INTERSECT",EDGE,{"derivedFrom":[makeQuery(id+"F37.opExtrude","CAP_FACE",FACE,{"disambiguationData":[OSD([sQuery(id+"F36.wireOp",EDGE,"E57.MirrorC")])],"isStart":false}),makeQuery(id+"F37.opExtrude","CAP_FACE",FACE,{"disambiguationData":[OSD([sQuery(id+"F36.wireOp",EDGE,"E84.MirrorC")])],"isStart":false}),makeQuery(id+"F37.opExtrude","CAP_FACE",FACE,{"disambiguationData":[OSD([sQuery(id+"F36.wireOp",EDGE,"E97.MirrorC")])],"isStart":false}),makeQuery(id+"F37.opExtrude","CAP_FACE",FACE,{"disambiguationData":[OSD([sQuery(id+"F36.wireOp",EDGE,"E101.MirrorC")])],"isStart":false})]});
            var Q19;
            Q19=makeQuery(id+"F30.opExtrude","CAP_EDGE",EDGE,{"disambiguationData":[OSD([sQuery(id+"F29.wireOp",EDGE,"E31")])],"isStart":false});
            var Q20;
            Q20=makeQuery(id+"F30.opExtrude","CAP_EDGE",EDGE,{"disambiguationData":[OSD([sQuery(id+"F29.wireOp",EDGE,"E43.right")])],"isStart":false});
            var Q21;
            Q21=makeQuery(id+"F37.boolean.opBoolean","INTERSECT",EDGE,{"derivedFrom":[makeQuery(id+"F37.opExtrude","CAP_FACE",FACE,{"disambiguationData":[OSD([sQuery(id+"F36.wireOp",EDGE,"E47")])],"isStart":false}),makeQuery(id+"F37.opExtrude","CAP_FACE",FACE,{"disambiguationData":[OSD([sQuery(id+"F36.wireOp",EDGE,"E48")])],"isStart":false}),makeQuery(id+"F37.opExtrude","CAP_FACE",FACE,{"disambiguationData":[OSD([sQuery(id+"F36.wireOp",EDGE,"E49")])],"isStart":false}),makeQuery(id+"F37.opExtrude","CAP_FACE",FACE,{"disambiguationData":[OSD([sQuery(id+"F36.wireOp",EDGE,"E50")])],"isStart":false})]});
            var Q22;
            Q22=makeQuery(id+"F30.opExtrude","CAP_EDGE",EDGE,{"disambiguationData":[OSD([sQuery(id+"F29.wireOp",EDGE,"E36")])],"isStart":false});
            var Q23;
            Q23=makeQuery(id+"F30.opExtrude","CAP_EDGE",EDGE,{"disambiguationData":[OSD([sQuery(id+"F29.wireOp",EDGE,"E42.right")])],"isStart":false});
            fillet(context, id + "F45", {"entities" : qUnion([Q0, Q1, Q2, Q3, Q4, Q5, Q6, Q7, Q8, Q9, Q10, Q11, Q12, Q13, Q14, Q15, Q16, Q17, Q18, Q19, Q20, Q21, Q22, Q23]), "radius" : 1 * mm, "tangentPropagation" : true, "allowEdgeOverflow" : false});
        }
        {
            var Q0;
            Q0=makeQuery(id+"F1.opExtrude","CAP_EDGE",EDGE,{"disambiguationData":[OSD([sQuery(id+"F0.wireOp",EDGE,"E0.top")])],"isStart":true});
            var Q1;
            Q1=makeQuery(id+"F1.opExtrude","CAP_EDGE",EDGE,{"disambiguationData":[OSD([sQuery(id+"F0.wireOp",EDGE,"E0.right")])],"isStart":true});
            var Q2;
            Q2=makeQuery(id+"F1.opExtrude","CAP_EDGE",EDGE,{"disambiguationData":[OSD([sQuery(id+"F0.wireOp",EDGE,"E0.left")])],"isStart":true});
            var Q3;
            Q3=makeQuery(id+"F1.opExtrude","CAP_EDGE",EDGE,{"disambiguationData":[OSD([sQuery(id+"F0.wireOp",EDGE,"E0.bottom")])],"isStart":true});
            var Q4;
            Q4=makeQuery(id+"F1.opExtrude","SWEPT_EDGE",EDGE,{"disambiguationData":[OSD([sQuery(id+"F0.wireOp",EDGE,"E0.bottom"),sQuery(id+"F0.wireOp",EDGE,"E0.left")])]});
            var Q5;
            Q5=makeQuery(id+"F1.opExtrude","SWEPT_EDGE",EDGE,{"disambiguationData":[OSD([sQuery(id+"F0.wireOp",EDGE,"E0.bottom"),sQuery(id+"F0.wireOp",EDGE,"E0.right")])]});
            var Q6;
            Q6=makeQuery(id+"F1.opExtrude","SWEPT_EDGE",EDGE,{"disambiguationData":[OSD([sQuery(id+"F0.wireOp",EDGE,"E0.top"),sQuery(id+"F0.wireOp",EDGE,"E0.right")])]});
            var Q7;
            Q7=makeQuery(id+"F1.opExtrude","SWEPT_EDGE",EDGE,{"disambiguationData":[OSD([sQuery(id+"F0.wireOp",EDGE,"E0.top"),sQuery(id+"F0.wireOp",EDGE,"E0.left")])]});
            var Q8;
            Q8=makeQuery(id+"F2.opShell","OFFSET_EDGE",EDGE,{"disambiguationData":[OSD([sQuery(id+"F0.wireOp",EDGE,"E0.top"),sQuery(id+"F0.wireOp",EDGE,"E0.left")])]});
            var Q9;
            Q9=makeQuery(id+"F2.opShell","OFFSET_EDGE",EDGE,{"disambiguationData":[OSD([sQuery(id+"F0.wireOp",EDGE,"E0.top"),sQuery(id+"F0.wireOp",EDGE,"E0.right")])]});
            var Q10;
            Q10=makeQuery(id+"F2.opShell","OFFSET_EDGE",EDGE,{"disambiguationData":[OSD([sQuery(id+"F0.wireOp",EDGE,"E0.bottom"),sQuery(id+"F0.wireOp",EDGE,"E0.left")])]});
            var Q11;
            Q11=makeQuery(id+"F2.opShell","OFFSET_EDGE",EDGE,{"disambiguationData":[OSD([sQuery(id+"F0.wireOp",EDGE,"E0.bottom"),sQuery(id+"F0.wireOp",EDGE,"E0.right")])]});
            fillet(context, id + "F46", {"entities" : qUnion([Q0, Q1, Q2, Q3, Q4, Q5, Q6, Q7, Q8, Q9, Q10, Q11]), "radius" : 7 * mm, "tangentPropagation" : true, "allowEdgeOverflow" : false});
        }
        {
            var Q0;
            Q0=makeQuery(id+"F26.boolean.opBoolean","MERGE",FACE,{"derivedFrom":[makeQuery(id+"F25.opExtrude","SWEPT_FACE",FACE,{"disambiguationData":[OSD([sQuery(id+"F24.wireOp",EDGE,"E25.top")])]}),makeQuery(id+"F26.opExtrude","SWEPT_FACE",FACE,{"disambiguationData":[OSD([sQuery(id+"F24.wireOp",EDGE,"E22.top")])]}),makeQuery(id+"F26.opExtrude","SWEPT_FACE",FACE,{"disambiguationData":[OSD([sQuery(id+"F24.wireOp",EDGE,"E23.top")])]})]});
            var sketch = newSketch(context, id + "F47", { "sketchPlane" : qUnion([Q0])});
            skArc(sketch, "E112", {"start": v(-6, 19) * mm, "mid": v(0, 13) * mm, "end": v(6, 19) * mm});
            skLineSegment(sketch, "E113", {"start": v(-6, 19) * mm, "end": v(-6, 13) * mm});
            skLineSegment(sketch, "E114", {"start": v(-6, 13) * mm, "end": v(6, 13) * mm});
            skLineSegment(sketch, "E115", {"start": v(6, 13) * mm, "end": v(6, 19) * mm});
            skSolve(sketch);
        }
        {
            var Q0;
            Q0 = qSketchRegion(id + "F47", true);
            extrude(context, id + "F48", {"entities" : qUnion([Q0]), "operationType" : NewBodyOperationType.ADD, "oppositeDirection" : true, "depth" : 14 * mm, "offsetDistance" : 25 * mm});
        }
    });
